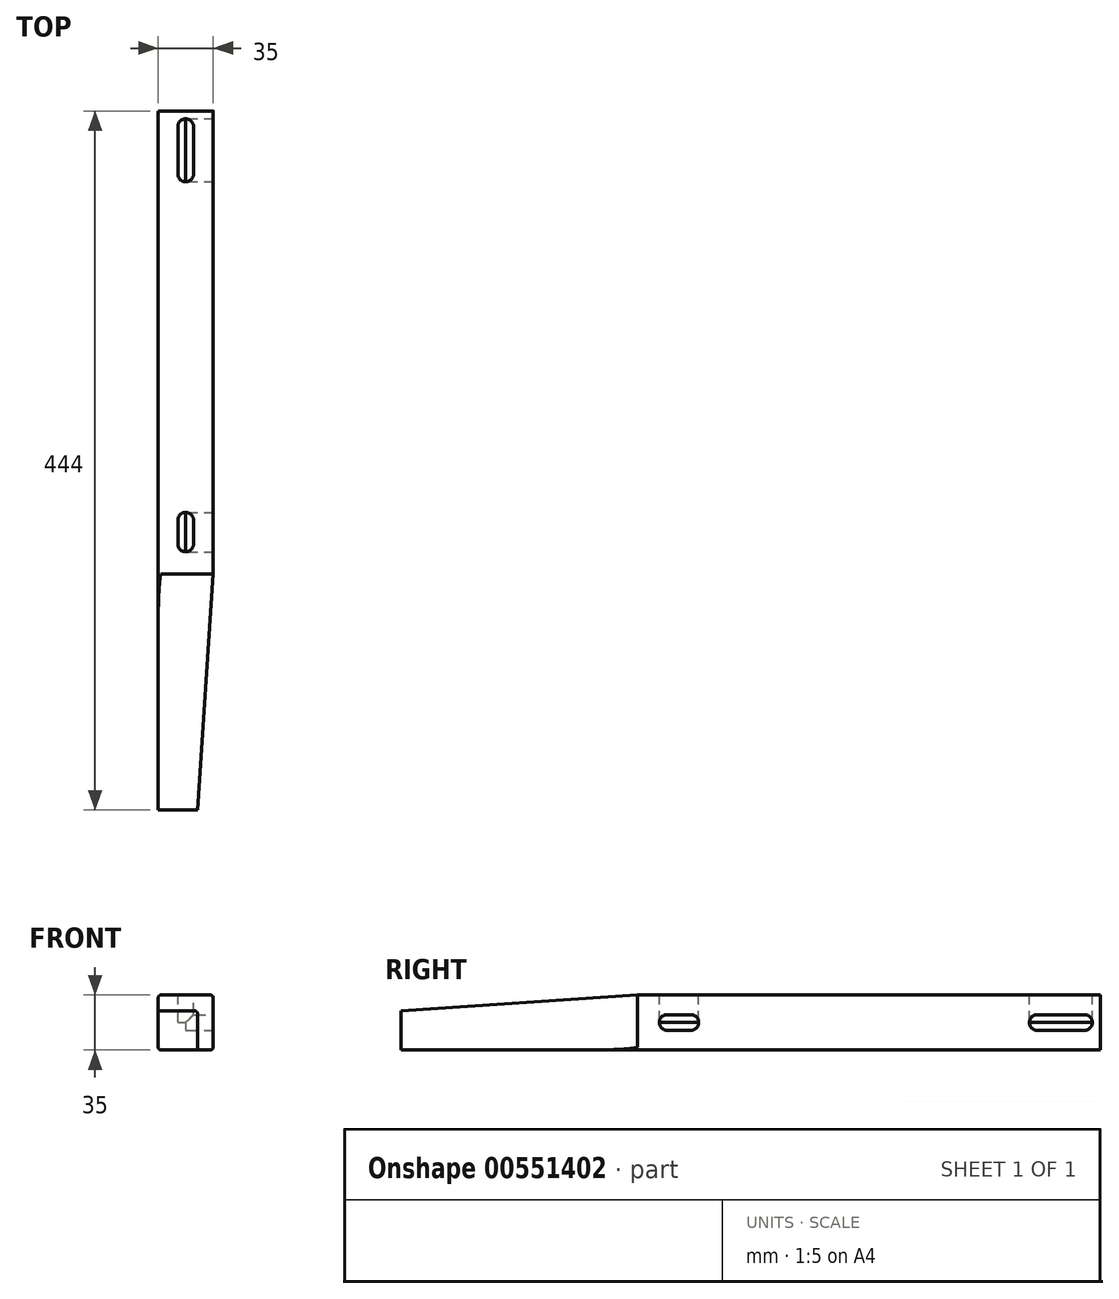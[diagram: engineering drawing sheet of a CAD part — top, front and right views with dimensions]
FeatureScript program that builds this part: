
annotation { "Feature Type Name" : "Feature", "Feature Type Description" : "" }
export const myFeature = defineFeature(function(context is Context, id is Id, definition is map)
    precondition{}
    {
        {
            var Q0;
            Q0=qCreatedBy(makeId("Front.planeOp"),FACE);
            var sketch = newSketch(context, id + "F0", { "sketchPlane" : qUnion([Q0])});
            skLineSegment(sketch, "E0.bottom", {"start": v(-17.5, -17.5) * mm, "end": v(17.5, -17.5) * mm});
            skLineSegment(sketch, "E0.top", {"start": v(-17.5, 17.5) * mm, "end": v(17.5, 17.5) * mm});
            skLineSegment(sketch, "E0.left", {"start": v(-17.5, -17.5) * mm, "end": v(-17.5, 17.5) * mm});
            skLineSegment(sketch, "E0.right", {"start": v(17.5, -17.5) * mm, "end": v(17.5, 17.5) * mm});
            skPoint(sketch, "E0.middle", {"position": v(0, 0) * mm});
            skSolve(sketch);
        }
        {
            var Q0;
            Q0=makeQuery(id+"F0.imprint","IMPRINT",FACE,{"disambiguationData":[TD([[makeQuery(id+"F0.imprint","IMPRINT",EDGE,{"derivedFrom":sQuery(id+"F0.wireOp",EDGE,"E0.bottom")}),1.0]])]});
            extrude(context, id + "F1", {"entities" : qUnion([Q0]), "depth" : 444 * mm, "offsetDistance" : 25 * mm});
        }
        {
            var Q0;
            Q0=makeQuery(id+"F1.opExtrude","SWEPT_FACE",FACE,{"disambiguationData":[OSD([sQuery(id+"F0.wireOp",EDGE,"E0.right")])]});
            var sketch = newSketch(context, id + "F2", { "sketchPlane" : qUnion([Q0])});
            skLineSegment(sketch, "E1.0.0", {"start": v(0, -17.5) * mm, "end": v(0, 17.5) * mm});
            skLineSegment(sketch, "E1.0.1", {"start": v(0, 17.5) * mm, "end": v(-444, 17.5) * mm});
            skLineSegment(sketch, "E1.0.2", {"start": v(-444, 17.5) * mm, "end": v(-444, -17.5) * mm});
            skLineSegment(sketch, "E1.0.3", {"start": v(-444, -17.5) * mm, "end": v(0, -17.5) * mm});
            skLineSegment(sketch, "E2", {"start": v(-444, 7.5) * mm, "end": v(-294, 17.5) * mm});
            skSolve(sketch);
        }
        {
            var Q0;
            {var subQ3=sQuery(id+"F2.wireOp",EDGE,"E2");Q0=makeQuery(id+"F2.imprint","IMPRINT",FACE,{"disambiguationData":[TD([[makeQuery(id+"F2.imprint","IMPRINT",EDGE,{"derivedFrom":subQ3}),1.0]])]});}
            extrude(context, id + "F3", {"entities" : qUnion([Q0]), "operationType" : NewBodyOperationType.REMOVE, "oppositeDirection" : true, "depth" : 35 * mm, "offsetDistance" : 25 * mm});
        }
        {
            var Q0;
            Q0=makeQuery(id+"F1.opExtrude","SWEPT_FACE",FACE,{"disambiguationData":[OSD([sQuery(id+"F0.wireOp",EDGE,"E0.top")])]});
            var sketch = newSketch(context, id + "F4", { "sketchPlane" : qUnion([Q0])});
            skLineSegment(sketch, "E3.0.0", {"start": v(-17.5, 0) * mm, "end": v(-17.5, -294) * mm});
            skLineSegment(sketch, "E3.0.1", {"start": v(-17.5, -294) * mm, "end": v(17.5, -294) * mm});
            skLineSegment(sketch, "E3.0.2", {"start": v(17.5, -294) * mm, "end": v(17.5, 0) * mm});
            skLineSegment(sketch, "E3.0.3", {"start": v(17.5, 0) * mm, "end": v(-17.5, 0) * mm});
            skLineSegment(sketch, "E4.0.0", {"start": v(17.5, -444) * mm, "end": v(17.5, -294) * mm});
            skLineSegment(sketch, "E4.0.1", {"start": v(17.5, -294) * mm, "end": v(-17.5, -294) * mm});
            skLineSegment(sketch, "E4.0.2", {"start": v(-17.5, -294) * mm, "end": v(-17.5, -444) * mm});
            skLineSegment(sketch, "E4.0.3", {"start": v(-17.5, -444) * mm, "end": v(17.5, -444) * mm});
            skLineSegment(sketch, "E5", {"start": v(17.5, -294) * mm, "end": v(7.5, -444) * mm});
            skSolve(sketch);
        }
        {
            var Q0;
            {var subQ0=sQuery(id+"F4.wireOp",EDGE,"E4.0.0");Q0=makeQuery(id+"F4.imprint","IMPRINT",FACE,{"disambiguationData":[TD([[makeQuery(id+"F4.imprint","IMPRINT",EDGE,{"derivedFrom":subQ0}),1.0]])]});}
            extrude(context, id + "F5", {"entities" : qUnion([Q0]), "operationType" : NewBodyOperationType.REMOVE, "oppositeDirection" : true, "depth" : 35 * mm, "offsetDistance" : 25 * mm});
        }
        {
            var Q0;
            Q0=makeQuery(id+"F1.opExtrude","SWEPT_FACE",FACE,{"disambiguationData":[OSD([sQuery(id+"F0.wireOp",EDGE,"E0.top")])]});
            var sketch = newSketch(context, id + "F6", { "sketchPlane" : qUnion([Q0])});
            skLineSegment(sketch, "E6.bottom", {"start": v(-5, -275) * mm, "end": v(5, -275) * mm});
            skLineSegment(sketch, "E6.top", {"start": v(-5, -260) * mm, "end": v(5, -260) * mm});
            skLineSegment(sketch, "E6.left", {"start": v(-5, -275) * mm, "end": v(-5, -260) * mm});
            skLineSegment(sketch, "E6.right", {"start": v(5, -275) * mm, "end": v(5, -260) * mm});
            skPoint(sketch, "E6.middle", {"position": v(0, -267.5) * mm});
            skLineSegment(sketch, "E7.bottom", {"start": v(-5, -40) * mm, "end": v(5, -40) * mm});
            skLineSegment(sketch, "E7.top", {"start": v(-5, -10) * mm, "end": v(5, -10) * mm});
            skLineSegment(sketch, "E7.left", {"start": v(-5, -40) * mm, "end": v(-5, -10) * mm});
            skLineSegment(sketch, "E7.right", {"start": v(5, -40) * mm, "end": v(5, -10) * mm});
            skPoint(sketch, "E7.middle", {"position": v(0, -25) * mm});
            skCircle(sketch, "E8", {"center": v(0, -275) * mm, "radius": 5 * mm});
            skCircle(sketch, "E9", {"center": v(0, -260) * mm, "radius": 5 * mm});
            skCircle(sketch, "E10", {"center": v(0, -40) * mm, "radius": 5 * mm});
            skCircle(sketch, "E11", {"center": v(0, -10) * mm, "radius": 5 * mm});
            skSolve(sketch);
        }
        {
            var Q0;
            Q0 = qSketchRegion(id + "F6", true);
            extrude(context, id + "F7", {"entities" : qUnion([Q0]), "operationType" : NewBodyOperationType.REMOVE, "oppositeDirection" : true, "depth" : 17.5 * mm, "offsetDistance" : 25 * mm});
        }
        {
            var Q0;
            Q0=makeQuery(id+"F1.opExtrude","SWEPT_FACE",FACE,{"disambiguationData":[OSD([sQuery(id+"F0.wireOp",EDGE,"E0.right")])]});
            var sketch = newSketch(context, id + "F8", { "sketchPlane" : qUnion([Q0])});
            skSolve(sketch);
        }
        {
            var Q0;
            {var subQ0=sQuery(id+"F0.wireOp",EDGE,"E0.right");Q0=makeQuery(id+"F8.imprint","IMPRINT",FACE,{"disambiguationData":[TD([[makeQuery(id+"F8.imprint","IMPRINT",EDGE,{"derivedFrom":makeQuery(id+"F1.opExtrude","CAP_EDGE",EDGE,{"disambiguationData":[OSD([subQ0])],"isStart":true})}),1.0]])]});}
            var sketch = newSketch(context, id + "F9", { "sketchPlane" : qUnion([Q0])});
            skLineSegment(sketch, "E12.bottom", {"start": v(-275, -5) * mm, "end": v(-260, -5) * mm});
            skLineSegment(sketch, "E12.top", {"start": v(-275, 5) * mm, "end": v(-260, 5) * mm});
            skLineSegment(sketch, "E12.left", {"start": v(-275, -5) * mm, "end": v(-275, 5) * mm});
            skLineSegment(sketch, "E12.right", {"start": v(-260, -5) * mm, "end": v(-260, 5) * mm});
            skPoint(sketch, "E12.middle", {"position": v(-267.5, 0) * mm});
            skLineSegment(sketch, "E13.bottom", {"start": v(-40, -5) * mm, "end": v(-10, -5) * mm});
            skLineSegment(sketch, "E13.top", {"start": v(-40, 5) * mm, "end": v(-10, 5) * mm});
            skLineSegment(sketch, "E13.left", {"start": v(-40, -5) * mm, "end": v(-40, 5) * mm});
            skLineSegment(sketch, "E13.right", {"start": v(-10, -5) * mm, "end": v(-10, 5) * mm});
            skPoint(sketch, "E13.middle", {"position": v(-25, 0) * mm});
            skCircle(sketch, "E14", {"center": v(-275, 0) * mm, "radius": 5 * mm});
            skCircle(sketch, "E15", {"center": v(-260, 0) * mm, "radius": 5 * mm});
            skCircle(sketch, "E16", {"center": v(-40, 0) * mm, "radius": 5 * mm});
            skCircle(sketch, "E17", {"center": v(-10, 0) * mm, "radius": 5 * mm});
            skSolve(sketch);
        }
        {
            var Q0;
            Q0 = qSketchRegion(id + "F9", true);
            extrude(context, id + "F10", {"entities" : qUnion([Q0]), "operationType" : NewBodyOperationType.REMOVE, "oppositeDirection" : true, "depth" : 17.5 * mm, "offsetDistance" : 25 * mm});
        }
        {
            var Q0;
            Q0=makeQuery(id+"F3.boolean.opBoolean","COPY",EDGE,{"derivedFrom":makeQuery(id+"F3.opExtrude","CAP_EDGE",EDGE,{"disambiguationData":[OSD([sQuery(id+"F2.wireOp",EDGE,"E2")])],"isStart":false})});
            var Q1;
            Q1=makeQuery(id+"F1.opExtrude","SWEPT_EDGE",EDGE,{"disambiguationData":[OSD([sQuery(id+"F0.wireOp",EDGE,"E0.top"),sQuery(id+"F0.wireOp",EDGE,"E0.left")])]});
            var Q2;
            Q2=makeQuery(id+"F1.opExtrude","SWEPT_EDGE",EDGE,{"disambiguationData":[OSD([sQuery(id+"F0.wireOp",EDGE,"E0.top"),sQuery(id+"F0.wireOp",EDGE,"E0.right")])]});
            var Q3;
            Q3=makeQuery(id+"F1.opExtrude","SWEPT_EDGE",EDGE,{"disambiguationData":[OSD([sQuery(id+"F0.wireOp",EDGE,"E0.bottom"),sQuery(id+"F0.wireOp",EDGE,"E0.right")])]});
            var Q4;
            Q4=makeQuery(id+"F5.boolean.opBoolean","COPY",EDGE,{"derivedFrom":makeQuery(id+"F5.opExtrude","CAP_EDGE",EDGE,{"disambiguationData":[OSD([sQuery(id+"F4.wireOp",EDGE,"E5")])],"isStart":false})});
            var Q5;
            Q5=makeQuery(id+"F5.boolean.opBoolean","INTERSECT",EDGE,{"derivedFrom":[makeQuery(id+"F3.boolean.opBoolean","COPY",FACE,{"derivedFrom":makeQuery(id+"F3.opExtrude","SWEPT_FACE",FACE,{"disambiguationData":[OSD([sQuery(id+"F2.wireOp",EDGE,"E2")])]})}),makeQuery(id+"F5.opExtrude","SWEPT_FACE",FACE,{"disambiguationData":[OSD([sQuery(id+"F4.wireOp",EDGE,"E5")])]})]});
            var Q6;
            Q6=makeQuery(id+"F1.opExtrude","SWEPT_EDGE",EDGE,{"disambiguationData":[OSD([sQuery(id+"F0.wireOp",EDGE,"E0.bottom"),sQuery(id+"F0.wireOp",EDGE,"E0.left")])]});
            fillet(context, id + "F11", {"entities" : qUnion([Q0, Q1, Q2, Q3, Q4, Q5, Q6]), "radius" : 2 * mm, "tangentPropagation" : true, "allowEdgeOverflow" : false});
        }
    });
